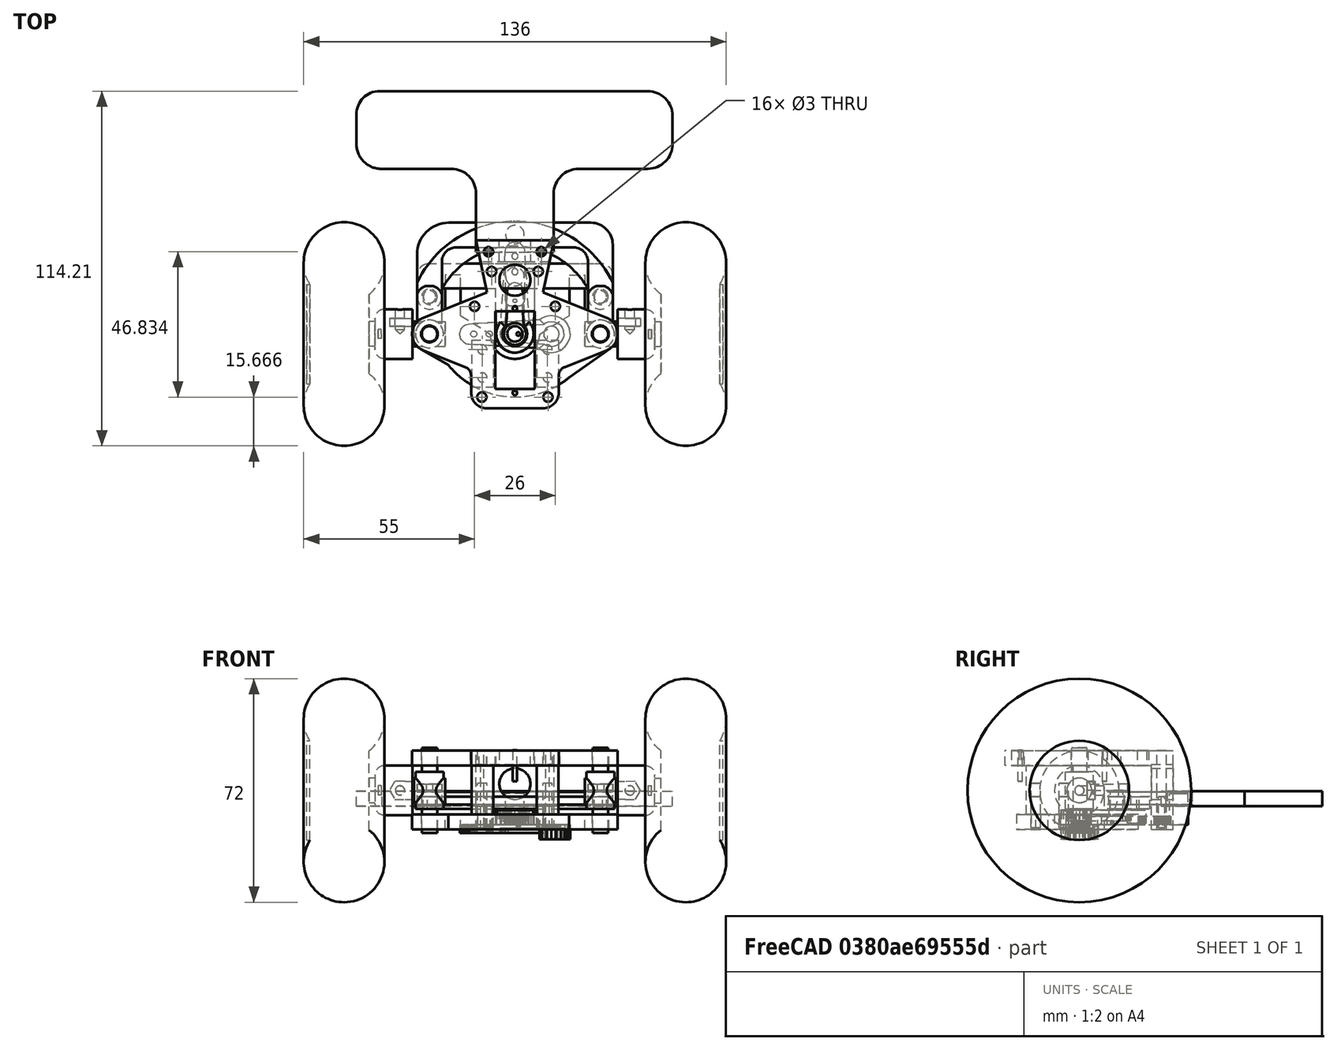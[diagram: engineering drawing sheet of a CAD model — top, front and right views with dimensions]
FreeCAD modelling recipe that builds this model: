
FCSTD DOCUMENT  (FreeCAD 0.18R16131 (Git))
Label: Direccion V2
License: All rights reserved
LicenseURL: http://en.wikipedia.org/wiki/All_rights_reserved
objects: Part::Cylinder×44, Part::MultiFuse×20, Sketcher::SketchObject×14, Part::Cut×10, PartDesign::Pad×9, Part::Feature×9, Part::Box×8, App::DocumentObjectGroup×7, Part::Fillet×6, Part::Extrusion×4, Mesh::Feature×2, Part::Torus×2, PartDesign::Pocket×1, PartDesign::Fillet×1
note: 138 computed .brp shape members not serialized (recipe doc carries the construction recipe); baked Part::Feature solids carry a one-line shape summary decoded from their .brp

FEATURE [Sketcher::SketchObject] Sketch  label="SketchB"
  MapMode = 5
  Placement = pos=(0,0,-1.5) rot=(0,0,1;0rad)
  sketch-geometry (23):
    g0: LineSegment StartX=-29.5785 StartY=5.19999 StartZ=0 EndX=-22.5 EndY=8.02935 EndZ=0
    g1: LineSegment StartX=22.5 StartY=8.02935 StartZ=0 EndX=29.5822 EndY=5.1985 EndZ=0
    g2: LineSegment StartX=30.743 StartY=-4.56538 StartZ=0 EndX=17.4375 EndY=-14.017 EndZ=0
    g3: LineSegment StartX=-21.4029 StartY=-10.0046 StartZ=0 EndX=-30.3074 EndY=-4.84546 EndZ=0
    g4: Circle CenterX=27.5 CenterY=0 CenterZ=0 NormalX=0 NormalY=0 NormalZ=1 AngleXU=0 Radius=2.7
    g5: Circle CenterX=-27.5 CenterY=0 CenterZ=0 NormalX=0 NormalY=0 NormalZ=1 AngleXU=0 Radius=2.7
    g6: ArcOfCircle CenterX=27.5 CenterY=0 CenterZ=0 NormalX=0 NormalY=0 NormalZ=1 AngleXU=0 Radius=5.6 StartAngle=5.33003 EndAngle=7.47301
    g7: ArcOfCircle CenterX=-27.5 CenterY=0 CenterZ=0 NormalX=0 NormalY=0 NormalZ=1 AngleXU=0 Radius=5.6 StartAngle=1.95105 EndAngle=4.18726
    g8: ArcOfCircle CenterX=0 CenterY=0 CenterZ=0 NormalX=0 NormalY=0 NormalZ=1 AngleXU=0 Radius=8 StartAngle=3.14159 EndAngle=6.28319
    g9: ArcOfCircle CenterX=0 CenterY=7.18175 CenterZ=0 NormalX=0 NormalY=0 NormalZ=1 AngleXU=0 Radius=27.4491 StartAngle=3.81816 EndAngle=5.40074
    g10: LineSegment StartX=-17.5 StartY=5.98295 StartZ=0 EndX=-8 EndY=-2.0002e-12 EndZ=0
    g11: LineSegment StartX=8 StartY=3e-12 StartZ=0 EndX=17.5 EndY=5.98295 EndZ=0
    g12: LineSegment StartX=-17.5 StartY=5.98295 StartZ=0 EndX=-17.5 EndY=18.983 EndZ=0
    g13: LineSegment StartX=-22.5 StartY=18.983 StartZ=0 EndX=-22.5 EndY=8.02935 EndZ=0
    g14: LineSegment StartX=-17.5 StartY=18.983 StartZ=0 EndX=-22.5 EndY=18.983 EndZ=0
    g15: LineSegment [constr] StartX=17.5 StartY=5.98295 StartZ=0 EndX=22.5 EndY=8.02935 EndZ=0
    g16: LineSegment StartX=17.5 StartY=5.98295 StartZ=0 EndX=17.5 EndY=18.983 EndZ=0
    g17: LineSegment StartX=17.5 StartY=18.983 StartZ=0 EndX=22.5 EndY=18.983 EndZ=0
    g18: LineSegment StartX=22.5 StartY=18.983 StartZ=0 EndX=22.5 EndY=8.02935 EndZ=0
    g19: Circle CenterX=10.5 CenterY=-4.99986 CenterZ=0 NormalX=0 NormalY=0 NormalZ=1 AngleXU=0 Radius=1.5
    g20: Circle CenterX=-10.5 CenterY=-4.99986 CenterZ=0 NormalX=0 NormalY=0 NormalZ=1 AngleXU=0 Radius=1.5
    g21: Circle CenterX=-10.5 CenterY=-13.9999 CenterZ=0 NormalX=0 NormalY=0 NormalZ=1 AngleXU=0 Radius=1.5
    g22: Circle CenterX=10.5 CenterY=-13.9999 CenterZ=0 NormalX=0 NormalY=0 NormalZ=1 AngleXU=0 Radius=1.5
  constraints (55):
    c: DistanceX(g5,g4) = 55
    c: Symmetric(g4,g5,g-2)
    c: PointOnObject(g4,g-1)
    c: Radius(g4) = 2.7
    c: Equal(g5,g4)
    c: Coincident(g6,g4)
    c: Coincident(g7,g5)
    c: Radius(g7) = 5.6
    c: Equal(g7,g6)
    c: DistanceY(g2,g11) = 20
    c: DistanceX(g10,g11) = 35
    c: Tangent(g2,g6) = 1.5708
    c: Tangent(g0,g7) = 1.5708
    c: Tangent(g3,g7) = 1.5708
    c: Coincident(g8,g-1)
    c: Radius(g8) = 8
    c: PointOnObject(g9,g-2)
    c: Coincident(g3,g9)
    c: PointOnObject(g8,g-1)
    c: PointOnObject(g8,g-1)
    c: Coincident(g10,g8)
    c: Coincident(g11,g8)
    c: Coincident(g12,g10)
    c: Vertical(g12)
    c: Vertical(g13)
    c: Coincident(g14,g12)
    c: Coincident(g14,g13)
    c: Horizontal(g14)
    c: Coincident(g0,g13)
    c: Symmetric(g10,g11,g-2)
    c: Symmetric(g1,g0,g-2)
    c: Coincident(g15,g11)
    c: Coincident(g6,g1)
    c: Coincident(g16,g11)
    c: Vertical(g16)
    c: PointOnObject(g18,g17)
    c: Vertical(g18)
    c: Coincident(g17,g18)
    c: DistanceX(g17,g17) = 5
    c: DistanceY(g16,g16) = 13
    c: Coincident(g16,g17)
    c: Horizontal(g17)
    c: Coincident(g15,g18)
    c: Coincident(g15,g1)
    c: Coincident(g9,g2)
    c: Equal(g12,g16)
    c: Radius(g19) = 1.5
    c: Equal(g19,g20)
    c: Equal(g20,g21)
    c: Equal(g21,g22)
    c: Symmetric(g20,g19,g-2)
    c: Symmetric(g21,g22,g-2)
    c: DistanceX(g20,g19) = 21
    c: DistanceX(g21,g22) = 21
    c: DistanceY(g21,g20) = 9
FEATURE [PartDesign::Pad] Pad  label="Carter superior"
  Length = 4.8
  Length2 = 100
  Placement = pos=(0,0,-1.5) rot=(0,0,1;0rad)
  Profile = -> Sketch
  Type = 0
FEATURE [Part::Cylinder] Cylinder  label="Cilindro"
  Angle = 360
  AttacherType = Attacher::AttachEngine3D
  Height = 27.5
  Placement = pos=(0,0,-13.75) rot=(0,0,1;0rad)
  Radius = 2.5
FEATURE [Part::Cylinder] Cylinder001  label="Cilindro001"
  Angle = 360
  AttacherType = Attacher::AttachEngine3D
  Height = 12
  Placement = pos=(0,0,-6) rot=(0,0,1;0rad)
  Radius = 4.5
FEATURE [Part::Cylinder] Cylinder002  label="Cilindro002"
  Angle = 360
  AttacherType = Attacher::AttachEngine3D
  Height = 10
  Placement = pos=(-5,0,0) rot=(0,1,0;1.5708rad)
  Radius = 4
FEATURE [Part::Cylinder] Cylinder003  label="Eje giro rueda 1"
  Angle = 360
  AttacherType = Attacher::AttachEngine3D
  Height = 20
  Placement = pos=(23,0,11) rot=(0,1,0;1.5708rad)
  Radius = 1.5
FEATURE [Part::Box] Box  label="Cubo"
  AttacherType = Attacher::AttachEngine3D
  Height = 2
  Length = 8
  Placement = pos=(-4,0,0) rot=(0,0,1;0rad)
  Width = 15.5
FEATURE [Sketcher::SketchObject] Sketch001
  MapMode = 5
  sketch-geometry (7):
    g0: ArcOfCircle CenterX=0 CenterY=11.4326 CenterZ=0 NormalX=0 NormalY=0 NormalZ=1 AngleXU=0 Radius=4.2 StartAngle=6.10025 EndAngle=9.60926
    g1: LineSegment StartX=4.12992 StartY=10.6686 StartZ=0 EndX=4.12444 EndY=10.639 EndZ=0
    g2: LineSegment StartX=4.12444 StartY=10.639 StartZ=0 EndX=5.59637 EndY=10.639 EndZ=0
    g3: LineSegment StartX=5.59637 StartY=10.639 StartZ=0 EndX=5.59637 EndY=16.9442 EndZ=0
    g4: LineSegment StartX=5.59637 StartY=16.9442 StartZ=0 EndX=-5.22917 EndY=16.9442 EndZ=0
    g5: LineSegment StartX=-5.22917 StartY=16.9442 StartZ=0 EndX=-5.22917 EndY=10.7807 EndZ=0
    g6: LineSegment StartX=-5.22917 StartY=10.7807 StartZ=0 EndX=-4.12873 EndY=10.6622 EndZ=0
  constraints (13):
    c: PointOnObject(g0,g-2)
    c: Radius(g0) = 4.2
    c: Tangent(g0,g1) = 1.5708
    c: Coincident(g1,g2)
    c: Horizontal(g2)
    c: Coincident(g2,g3)
    c: Vertical(g3)
    c: Coincident(g3,g4)
    c: Horizontal(g4)
    c: Coincident(g4,g5)
    c: Vertical(g5)
    c: Coincident(g5,g6)
    c: Coincident(g6,g0)
FEATURE [PartDesign::Pad] Pad001
  Length = 10
  Length2 = 100
  Profile = -> Sketch001
  Type = 0
FEATURE [Part::Cut] Cut
  Base = -> Box
  Tool = -> Pad001
FEATURE [Part::Cylinder] Cylinder004  label="Cilindro004"
  Angle = 360
  AttacherType = Attacher::AttachEngine3D
  Height = 7.5
  Placement = pos=(0,12,-6) rot=(0,0,1;0rad)
  Radius = 2
FEATURE [Part::Cylinder] Cylinder005  label="Cilindro005"
  Angle = 360
  AttacherType = Attacher::AttachEngine3D
  Height = 27.5
  Placement = pos=(0,0,-13.75) rot=(0,0,1;0rad)
  Radius = 2.5
FEATURE [Part::Cylinder] Cylinder006  label="Cilindro006"
  Angle = 360
  AttacherType = Attacher::AttachEngine3D
  Height = 12
  Placement = pos=(0,0,-6) rot=(0,0,1;0rad)
  Radius = 4.5
FEATURE [Part::Cylinder] Cylinder007  label="Cilindro007"
  Angle = 360
  AttacherType = Attacher::AttachEngine3D
  Height = 10
  Placement = pos=(-5,0,0) rot=(0,1,0;1.5708rad)
  Radius = 4
FEATURE [Part::Box] Box001  label="Cubo001"
  AttacherType = Attacher::AttachEngine3D
  Height = 2
  Length = 8
  Placement = pos=(-4,0,0) rot=(0,0,1;0rad)
  Width = 15.5
FEATURE [Sketcher::SketchObject] Sketch002
  MapMode = 5
  sketch-geometry (7):
    g0: ArcOfCircle CenterX=0 CenterY=11.4326 CenterZ=0 NormalX=0 NormalY=0 NormalZ=1 AngleXU=0 Radius=4.2 StartAngle=6.10025 EndAngle=9.60926
    g1: LineSegment StartX=4.12992 StartY=10.6686 StartZ=0 EndX=4.12444 EndY=10.639 EndZ=0
    g2: LineSegment StartX=4.12444 StartY=10.639 StartZ=0 EndX=5.59637 EndY=10.639 EndZ=0
    g3: LineSegment StartX=5.59637 StartY=10.639 StartZ=0 EndX=5.59637 EndY=16.9442 EndZ=0
    g4: LineSegment StartX=5.59637 StartY=16.9442 StartZ=0 EndX=-5.22917 EndY=16.9442 EndZ=0
    g5: LineSegment StartX=-5.22917 StartY=16.9442 StartZ=0 EndX=-5.22917 EndY=10.7807 EndZ=0
    g6: LineSegment StartX=-5.22917 StartY=10.7807 StartZ=0 EndX=-4.12873 EndY=10.6622 EndZ=0
  constraints (13):
    c: PointOnObject(g0,g-2)
    c: Radius(g0) = 4.2
    c: Tangent(g0,g1) = 1.5708
    c: Coincident(g1,g2)
    c: Horizontal(g2)
    c: Coincident(g2,g3)
    c: Vertical(g3)
    c: Coincident(g3,g4)
    c: Horizontal(g4)
    c: Coincident(g4,g5)
    c: Vertical(g5)
    c: Coincident(g5,g6)
    c: Coincident(g6,g0)
FEATURE [PartDesign::Pad] Pad002
  Length = 10
  Length2 = 100
  Profile = -> Sketch002
  Type = 0
FEATURE [Part::Cut] Cut001
  Base = -> Box001
  Tool = -> Pad002
FEATURE [Part::Cylinder] Cylinder008  label="Cilindro008"
  Angle = 360
  AttacherType = Attacher::AttachEngine3D
  Height = 7.5
  Placement = pos=(0,12,-6) rot=(0,0,1;0rad)
  Radius = 2
FEATURE [Part::Cylinder] Cylinder009  label="Eje giro rueda 2"
  Angle = 360
  AttacherType = Attacher::AttachEngine3D
  Height = 20
  Placement = pos=(-43,0,11) rot=(0,1,0;1.5708rad)
  Radius = 1.5
FEATURE [Part::MultiFuse] Fusion  label="Eje giro direccion 1"
  Placement = pos=(27.5,0,11) rot=(0,0,1;0rad)
  Shapes = -> [Cylinder,Cylinder001,Cylinder002,Cut,Cylinder004]
FEATURE [Part::MultiFuse] Fusion001  label="Eje giro direccion 2"
  Placement = pos=(-27.5,0,11) rot=(0,0,1;0rad)
  Shapes = -> [Cylinder005,Cylinder006,Cylinder007,Cut001,Cylinder008]
FEATURE [Sketcher::SketchObject] Sketch003
  MapMode = 5
  Placement = pos=(0,12,1.5) rot=(0,0,1;0rad)
  Support = -> [Cylinder008]
  sketch-geometry (12):
    g0: LineSegment StartX=-23.5 StartY=0 StartZ=0 EndX=-23.5 EndY=11.3304 EndZ=0
    g1: LineSegment StartX=-18.9625 StartY=15.8679 StartZ=0 EndX=18.9404 EndY=15.8679 EndZ=0
    g2: LineSegment StartX=23.5 StartY=11.3083 StartZ=0 EndX=23.5 EndY=0 EndZ=0
    g3: LineSegment StartX=31.5 StartY=0 StartZ=0 EndX=31.5 EndY=16.7855 EndZ=0
    g4: LineSegment StartX=24.4177 StartY=23.8679 StartZ=0 EndX=-21.2655 EndY=23.8679 EndZ=0
    g5: LineSegment StartX=-31.5 StartY=13.6334 StartZ=0 EndX=-31.5 EndY=0 EndZ=0
    g6: ArcOfCircle CenterX=27.5 CenterY=0 CenterZ=0 NormalX=0 NormalY=0 NormalZ=1 AngleXU=0 Radius=4 StartAngle=3.14159 EndAngle=6.28319
    g7: ArcOfCircle CenterX=-27.5 CenterY=0 CenterZ=0 NormalX=0 NormalY=0 NormalZ=1 AngleXU=0 Radius=4 StartAngle=3.14159 EndAngle=6.28319
    g8: ArcOfCircle CenterX=-21.2655 CenterY=13.6334 CenterZ=0 NormalX=0 NormalY=0 NormalZ=1 AngleXU=0 Radius=10.2345 StartAngle=1.5708 EndAngle=3.14159
    g9: ArcOfCircle CenterX=-18.9625 CenterY=11.3304 CenterZ=0 NormalX=0 NormalY=0 NormalZ=1 AngleXU=0 Radius=4.53751 StartAngle=1.5708 EndAngle=3.14159
    g10: ArcOfCircle CenterX=24.4177 CenterY=16.7855 CenterZ=0 NormalX=0 NormalY=0 NormalZ=1 AngleXU=0 Radius=7.08234 StartAngle=0 EndAngle=1.5708
    g11: ArcOfCircle CenterX=18.9404 CenterY=11.3083 CenterZ=0 NormalX=0 NormalY=0 NormalZ=1 AngleXU=0 Radius=4.55958 StartAngle=0 EndAngle=1.5708
  constraints (30):
    c: Vertical(g0)
    c: Horizontal(g1)
    c: Vertical(g3)
    c: Horizontal(g4)
    c: Vertical(g5)
    c: DistanceX(g5,g0) = 8
    c: Vertical(g2)
    c: PointOnObject(g6,g-1)
    c: Tangent(g6,g3) = -1.5708
    c: Coincident(g3,g6)
    c: Tangent(g6,g2) = -1.5708
    c: Radius(g6) = 4
    c: Coincident(g2,g6)
    c: PointOnObject(g7,g-1)
    c: Tangent(g7,g5) = -1.5708
    c: Tangent(g7,g0) = -1.5708
    c: Coincident(g5,g7)
    c: Coincident(g0,g7)
    c: Radius(g7) = 4
    c: Tangent(g5,g8) = -1.5708
    c: Tangent(g4,g8) = -1.5708
    c: Tangent(g0,g9) = 1.5708
    c: Tangent(g1,g9) = 1.5708
    c: Tangent(g3,g10) = -1.5708
    c: Tangent(g4,g10) = -1.5708
    c: Tangent(g2,g11) = 1.5708
    c: Tangent(g1,g11) = 1.5708
    c: DistanceY(g1,g4) = 8
    c: Symmetric(g5,g3,g-2)
    c: DistanceX(g0,g2) = 47
FEATURE [Part::Extrusion] Extrude  label="Barra direccion"
  Base = -> Sketch003
  Dir = (0,0,4)
  DirMode = 0
  FaceMakerClass = Part::FaceMakerExtrusion
  LengthFwd = 0
  LengthRev = 0
  Placement = pos=(0,0,5) rot=(0,0,1;0rad)
  Solid = true
  Symmetric = false
FEATURE [Part::Cylinder] Cylinder010  label="Cilindro009"
  Angle = 360
  AttacherType = Attacher::AttachEngine3D
  Height = 7.5
  Placement = pos=(-27.5,12,5) rot=(0,0,1;0rad)
  Radius = 2.5
FEATURE [Part::Cylinder] Cylinder011  label="Cilindro010"
  Angle = 360
  AttacherType = Attacher::AttachEngine3D
  Height = 7.5
  Placement = pos=(27.5,12,5) rot=(0,0,1;0rad)
  Radius = 2.5
FEATURE [Part::MultiFuse] Fusion002
  Shapes = -> [Cylinder010,Cylinder011]
FEATURE [Part::Cut] Cut002  label="Barra Dir"
  Base = -> Extrude
  Tool = -> Fusion002
FEATURE [Mesh::Feature] Servo_SG90  label="Servo-SG90"
  Placement = pos=(0,-16.5,33.5) rot=(0,1,0;3.14159rad)
FEATURE [Part::Cylinder] Cylinder012  label="Cilindro011"
  Angle = 360
  AttacherType = Attacher::AttachEngine3D
  Height = 20
  Placement = pos=(47,0,11) rot=(0,1,0;1.5708rad)
  Radius = 16
FEATURE [Part::Cylinder] Cylinder013  label="Cilindro012"
  Angle = 360
  AttacherType = Attacher::AttachEngine3D
  Height = 20
  Placement = pos=(-67,0,11) rot=(0,1,0;1.5708rad)
  Radius = 16
FEATURE [Part::Torus] Torus  label="Toro"
  Angle1 = -180
  Angle2 = 180
  Angle3 = 360
  AttacherType = Attacher::AttachEngine3D
  Placement = pos=(-55,0,11) rot=(0,1,0;1.5708rad)
  Radius1 = 23
  Radius2 = 13
FEATURE [Part::Torus] Torus001  label="Toro001"
  Angle1 = -180
  Angle2 = 180
  Angle3 = 360
  AttacherType = Attacher::AttachEngine3D
  Placement = pos=(55,0,11) rot=(0,1,0;1.5708rad)
  Radius1 = 23
  Radius2 = 13
FEATURE [Part::Cylinder] Cylinder014  label="Cilindro013"
  Angle = 360
  AttacherType = Attacher::AttachEngine3D
  Height = 12
  Radius = 8
FEATURE [Part::Cylinder] Cylinder015  label="Taladro"
  Angle = 360
  AttacherType = Attacher::AttachEngine3D
  Height = 11
  Radius = 1.5
FEATURE [Part::Cylinder] Cylinder016  label="Cilindro014"
  Angle = 360
  AttacherType = Attacher::AttachEngine3D
  Height = 2
  Placement = pos=(0,0,12) rot=(0,0,1;0rad)
  Radius = 4
FEATURE [Part::Box] Box002  label="Cubo002"
  AttacherType = Attacher::AttachEngine3D
  Height = 15
  Length = 1.7
  Placement = pos=(-0.85,-2.3,22) rot=(0,0,1;0rad)
  Width = 4.6
FEATURE [Part::Box] Box003  label="Cubo003"
  AttacherType = Attacher::AttachEngine3D
  Height = 15
  Length = 4.6
  Placement = pos=(-2.3,-0.85,22) rot=(0,0,1;0rad)
  Width = 1.7
FEATURE [Part::Fillet] Fillet
  Base = -> Box002
  Edges = 2 edges r=1: [Edge10,Edge12]
FEATURE [Part::Fillet] Fillet001
  Base = -> Box003
  Edges = 2 edges r=1: [Edge2,Edge6]
FEATURE [Part::MultiFuse] Fusion003
  Placement = pos=(0,0,-8) rot=(0,0,1;0rad)
  Shapes = -> [Fillet,Fillet001]
FEATURE [Part::Cylinder] Cylinder017  label="Taladro tornillo"
  Angle = 360
  AttacherType = Attacher::AttachEngine3D
  Height = 10
  Placement = pos=(0,0,4) rot=(-1,0,0;1.5708rad)
  Radius = 1.5
FEATURE [Sketcher::SketchObject] Sketch004
  MapMode = 5
  Placement = pos=(0,5,-2) rot=(1,0,0;1.5708rad)
  sketch-geometry (8):
    g0: LineSegment StartX=0 StartY=9.41258 StartZ=0 EndX=-2.88764 EndY=7.71686 EndZ=0
    g1: LineSegment StartX=-2.88764 StartY=7.71686 StartZ=0 EndX=-2.86293 EndY=4.36823 EndZ=0
    g2: LineSegment StartX=2.93707 StartY=4.41103 StartZ=0 EndX=2.91236 EndY=7.75966 EndZ=0
    g3: LineSegment StartX=2.91236 StartY=7.75966 StartZ=0 EndX=0 EndY=9.41258 EndZ=0
    g4: Circle [constr] CenterX=0.0247135 CenterY=6.06395 CenterZ=0 NormalX=0 NormalY=0 NormalZ=1 AngleXU=0 Radius=3.34872
    g5: LineSegment StartX=-2.86293 StartY=4.36823 StartZ=0 EndX=-2.86293 EndY=0 EndZ=0
    g6: LineSegment StartX=2.93707 StartY=4.41103 StartZ=0 EndX=2.93707 EndY=0 EndZ=0
    g7: LineSegment StartX=-2.86293 StartY=0 StartZ=0 EndX=2.93707 EndY=0 EndZ=0
  constraints (22):
    c: Coincident(g0,g1)
    c: Coincident(g2,g3)
    c: Coincident(g3,g0)
    c: Equal(g0,g1)
    c: Equal(g0,g2)
    c: Equal(g0,g3)
    c: PointOnObject(g0,g4)
    c: PointOnObject(g1,g4)
    c: PointOnObject(g2,g4)
    c: PointOnObject(g2,g4)
    c: PointOnObject(g3,g4)
    c: PointOnObject(g0,g-2)
    c: DistanceX(g0,g2) = 5.8
    c: Symmetric(g1,g2,g4)
    c: Coincident(g5,g1)
    c: PointOnObject(g5,g-1)
    c: Vertical(g5)
    c: Vertical(g6)
    c: Coincident(g7,g5)
    c: Coincident(g7,g6)
    c: Horizontal(g7)
    c: Coincident(g6,g2)
FEATURE [PartDesign::Pad] Pad003  label="Tuerca"
  Length = 2.5
  Length2 = 100
  Placement = pos=(0,5,-2) rot=(1,0,0;1.5708rad)
  Profile = -> Sketch004
  Type = 0
FEATURE [Part::MultiFuse] Fusion004  label="Hueco"
  Shapes = -> [Cylinder015,Cylinder017,Pad003]
FEATURE [Part::Fillet] Fillet002  label="Base"
  Base = -> Cylinder014
  Edges = 1 edges r=3: [Edge1]
FEATURE [Part::Cut] Cut003  label="Base2"
  Base = -> Fillet002
  Tool = -> Fusion004
FEATURE [Part::MultiFuse] Fusion005  label="Eje rueda delantera 1"
  Placement = pos=(33,0,11) rot=(0,1,0;1.5708rad)
  Shapes = -> [Cut003,Cylinder016,Fusion003]
FEATURE [Part::Cylinder] Cylinder018  label="Cilindro015"
  Angle = 360
  AttacherType = Attacher::AttachEngine3D
  Height = 12
  Radius = 8
FEATURE [Part::Cylinder] Cylinder019  label="Taladro001"
  Angle = 360
  AttacherType = Attacher::AttachEngine3D
  Height = 11
  Radius = 1.5
FEATURE [Part::Cylinder] Cylinder020  label="Cilindro016"
  Angle = 360
  AttacherType = Attacher::AttachEngine3D
  Height = 2
  Placement = pos=(0,0,12) rot=(0,0,1;0rad)
  Radius = 4
FEATURE [Part::Box] Box004  label="Cubo004"
  AttacherType = Attacher::AttachEngine3D
  Height = 15
  Length = 1.7
  Placement = pos=(-0.85,-2.3,22) rot=(0,0,1;0rad)
  Width = 4.6
FEATURE [Part::Box] Box005  label="Cubo005"
  AttacherType = Attacher::AttachEngine3D
  Height = 15
  Length = 4.6
  Placement = pos=(-2.3,-0.85,22) rot=(0,0,1;0rad)
  Width = 1.7
FEATURE [Part::Fillet] Fillet003
  Base = -> Box004
  Edges = 2 edges r=1: [Edge10,Edge12]
FEATURE [Part::Fillet] Fillet004
  Base = -> Box005
  Edges = 2 edges r=1: [Edge2,Edge6]
FEATURE [Part::MultiFuse] Fusion006
  Placement = pos=(0,0,-8) rot=(0,0,1;0rad)
  Shapes = -> [Fillet003,Fillet004]
FEATURE [Part::Cylinder] Cylinder021  label="Taladro tornillo001"
  Angle = 360
  AttacherType = Attacher::AttachEngine3D
  Height = 10
  Placement = pos=(0,0,4) rot=(-1,0,0;1.5708rad)
  Radius = 1.5
FEATURE [Sketcher::SketchObject] Sketch005
  MapMode = 5
  Placement = pos=(0,5,-2) rot=(1,0,0;1.5708rad)
  sketch-geometry (8):
    g0: LineSegment StartX=0 StartY=9.41258 StartZ=0 EndX=-2.88764 EndY=7.71686 EndZ=0
    g1: LineSegment StartX=-2.88764 StartY=7.71686 StartZ=0 EndX=-2.86293 EndY=4.36823 EndZ=0
    g2: LineSegment StartX=2.93707 StartY=4.41103 StartZ=0 EndX=2.91236 EndY=7.75966 EndZ=0
    g3: LineSegment StartX=2.91236 StartY=7.75966 StartZ=0 EndX=0 EndY=9.41258 EndZ=0
    g4: Circle [constr] CenterX=0.0247135 CenterY=6.06395 CenterZ=0 NormalX=0 NormalY=0 NormalZ=1 AngleXU=0 Radius=3.34872
    g5: LineSegment StartX=-2.86293 StartY=4.36823 StartZ=0 EndX=-2.86293 EndY=0 EndZ=0
    g6: LineSegment StartX=2.93707 StartY=4.41103 StartZ=0 EndX=2.93707 EndY=0 EndZ=0
    g7: LineSegment StartX=-2.86293 StartY=0 StartZ=0 EndX=2.93707 EndY=0 EndZ=0
  constraints (22):
    c: Coincident(g0,g1)
    c: Coincident(g2,g3)
    c: Coincident(g3,g0)
    c: Equal(g0,g1)
    c: Equal(g0,g2)
    c: Equal(g0,g3)
    c: PointOnObject(g0,g4)
    c: PointOnObject(g1,g4)
    c: PointOnObject(g2,g4)
    c: PointOnObject(g2,g4)
    c: PointOnObject(g3,g4)
    c: PointOnObject(g0,g-2)
    c: DistanceX(g0,g2) = 5.8
    c: Symmetric(g1,g2,g4)
    c: Coincident(g5,g1)
    c: PointOnObject(g5,g-1)
    c: Vertical(g5)
    c: Vertical(g6)
    c: Coincident(g7,g5)
    c: Coincident(g7,g6)
    c: Horizontal(g7)
    c: Coincident(g6,g2)
FEATURE [PartDesign::Pad] Pad004  label="Tuerca001"
  Length = 2.5
  Length2 = 100
  Placement = pos=(0,5,-2) rot=(1,0,0;1.5708rad)
  Profile = -> Sketch005
  Type = 0
FEATURE [Part::MultiFuse] Fusion007  label="Hueco001"
  Shapes = -> [Cylinder019,Cylinder021,Pad004]
FEATURE [Part::Fillet] Fillet005  label="Base003"
  Base = -> Cylinder018
  Edges = 1 edges r=3: [Edge1]
FEATURE [Part::Cut] Cut004  label="Base004"
  Base = -> Fillet005
  Tool = -> Fusion007
FEATURE [Part::MultiFuse] Fusion008  label="Eje rueda delantera 2"
  Placement = pos=(-33,0,11) rot=(0,-1,0;1.5708rad)
  Shapes = -> [Cut004,Cylinder020,Fusion006]
FEATURE [Part::MultiFuse] Fusion009
  Placement = pos=(3.6e-15,1.07e-14,0) rot=(0,0,1;0rad)
  Shapes = -> [Cylinder013,Torus,Fusion001,Cylinder009,Fusion008]
FEATURE [App::DocumentObjectGroup] Grupo001  label="Rueda 2"
  Group = -> [Fusion009]
FEATURE [Part::MultiFuse] Fusion010
  Placement = pos=(-3.6e-15,-1.07e-14,0) rot=(0,0,1;0rad)
  Shapes = -> [Cylinder012,Torus001,Fusion,Cylinder003,Fusion005]
FEATURE [App::DocumentObjectGroup] Grupo  label="Rueda 1"
  Group = -> [Fusion010]
FEATURE [Sketcher::SketchObject] Sketch006
  MapMode = 5
  Placement = pos=(0,12,1.5) rot=(0,0,1;0rad)
  Support = -> [Cylinder008]
  sketch-geometry (13):
    g0: ArcOfCircle CenterX=27.5 CenterY=0 CenterZ=0 NormalX=0 NormalY=0 NormalZ=1 AngleXU=0 Radius=4 StartAngle=3.14159 EndAngle=6.28319
    g1: ArcOfCircle CenterX=-27.5 CenterY=0 CenterZ=0 NormalX=0 NormalY=0 NormalZ=1 AngleXU=0 Radius=4 StartAngle=3.14159 EndAngle=6.28319
    g2: GeomPoint [constr] X=-0.022332 Y=22.2995 Z=0
    g3: GeomPoint [constr] X=0.308692 Y=14.2995 Z=0
    g4: GeomPoint [constr] X=0 Y=-10.7005 Z=0
    g5: GeomPoint [constr] X=0 Y=-2.70048 Z=0
    g6: LineSegment [constr] StartX=-48.5447 StartY=24.2365 StartZ=0 EndX=42.467 EndY=24.2365 EndZ=0
    g7: ArcOfCircle CenterX=0 CenterY=-10.7005 CenterZ=0 NormalX=0 NormalY=0 NormalZ=1 AngleXU=0 Radius=27 StartAngle=0.514842 EndAngle=2.62675
    g8: ArcOfCircle CenterX=0 CenterY=-10.7005 CenterZ=0 NormalX=0 NormalY=0 NormalZ=1 AngleXU=0 Radius=35 StartAngle=0.451027 EndAngle=2.69057
    g9: LineSegment StartX=-31.5 StartY=0 StartZ=0 EndX=-31.5 EndY=4.55567 EndZ=0
    g10: LineSegment StartX=-23.5 StartY=0 StartZ=0 EndX=-23.5 EndY=2.59426 EndZ=0
    g11: LineSegment StartX=23.5 StartY=0 StartZ=0 EndX=23.5 EndY=2.59426 EndZ=0
    g12: LineSegment StartX=31.5 StartY=0 StartZ=0 EndX=31.5 EndY=4.55567 EndZ=0
  constraints (28):
    c: DistanceX(g1,g1) = 8
    c: PointOnObject(g0,g-1)
    c: Radius(g0) = 4
    c: PointOnObject(g1,g-1)
    c: Symmetric(g1,g0,g-2)
    c: DistanceX(g1,g0) = 47
    c: PointOnObject(g4,g-2)
    c: DistanceY(g4,g3) = 25
    c: DistanceY(g3,g2) = 8
    c: Horizontal(g6)
    c: DistanceY(g4,g5) = 8
    c: PointOnObject(g5,g-2)
    c: Coincident(g7,g4)
    c: Coincident(g8,g4)
    c: Radius(g7) = 27
    c: Radius(g8) = 35
    c: Coincident(g9,g1)
    c: Vertical(g9)
    c: Coincident(g10,g1)
    c: Vertical(g10)
    c: Coincident(g11,g0)
    c: Vertical(g11)
    c: Coincident(g12,g0)
    c: Vertical(g12)
    c: Coincident(g12,g8)
    c: Coincident(g11,g7)
    c: Coincident(g7,g10)
    c: Coincident(g9,g8)
FEATURE [Part::Extrusion] Extrude001
  Base = -> Sketch006
  Dir = (0,0,4)
  DirMode = 0
  FaceMakerClass = Part::FaceMakerExtrusion
  LengthFwd = 0
  LengthRev = 0
  Placement = pos=(0,0,5) rot=(0,0,1;0rad)
  Solid = true
  Symmetric = false
FEATURE [Part::Cylinder] Cylinder022  label="Cilindro017"
  Angle = 360
  AttacherType = Attacher::AttachEngine3D
  Height = 7.5
  Placement = pos=(-27.5,12,5) rot=(0,0,1;0rad)
  Radius = 2.5
FEATURE [Part::Cylinder] Cylinder023  label="Cilindro018"
  Angle = 360
  AttacherType = Attacher::AttachEngine3D
  Height = 7.5
  Placement = pos=(27.5,12,5) rot=(0,0,1;0rad)
  Radius = 2.5
FEATURE [Part::MultiFuse] Fusion011
  Shapes = -> [Cylinder022,Cylinder023]
FEATURE [Part::Cut] Cut005
  Base = -> Extrude001
  Tool = -> Fusion011
FEATURE [Part::Cylinder] Cylinder024  label="Cilindro019"
  Angle = 360
  AttacherType = Attacher::AttachEngine3D
  Height = 10
  Placement = pos=(0,32,0) rot=(0,0,1;0rad)
  Radius = 3
FEATURE [App::DocumentObjectGroup] Grupo002  label="Barra direccion 2"
  Group = -> [Cut005,Cylinder024]
FEATURE [Sketcher::SketchObject] Sketch007
  MapMode = 5
  Placement = pos=(0,12,1.5) rot=(0,0,1;0rad)
  Support = -> [Cylinder008]
  sketch-geometry (10):
    g0: ArcOfCircle CenterX=27.5 CenterY=0 CenterZ=0 NormalX=0 NormalY=0 NormalZ=1 AngleXU=0 Radius=4 StartAngle=3.14159 EndAngle=6.28319
    g1: ArcOfCircle CenterX=-27.5 CenterY=0 CenterZ=0 NormalX=0 NormalY=0 NormalZ=1 AngleXU=0 Radius=4 StartAngle=3.14159 EndAngle=6.28319
    g2: LineSegment StartX=-23.5 StartY=2.66215 StartZ=0 EndX=23.5 EndY=2.66215 EndZ=0
    g3: LineSegment StartX=-28.1833 StartY=10.6622 StartZ=0 EndX=28.1833 EndY=10.6622 EndZ=0
    g4: LineSegment StartX=23.5 StartY=-1e-12 StartZ=0 EndX=23.5 EndY=2.66215 EndZ=0
    g5: LineSegment StartX=-23.5 StartY=0 StartZ=0 EndX=-23.5 EndY=2.66215 EndZ=0
    g6: LineSegment StartX=-31.5 StartY=2e-12 StartZ=0 EndX=-31.5 EndY=6.49244 EndZ=0
    g7: LineSegment StartX=31.5 StartY=2e-12 StartZ=0 EndX=31.5 EndY=7.29309 EndZ=0
    g8: ArcOfCircle CenterX=27.5422 CenterY=6.71386 CenterZ=0 NormalX=0 NormalY=0 NormalZ=1 AngleXU=0 Radius=4 StartAngle=0.145318 EndAngle=1.40983
    g9: ArcOfCircle CenterX=-27.5065 CenterY=6.71983 CenterZ=0 NormalX=0 NormalY=0 NormalZ=1 AngleXU=0 Radius=4 StartAngle=1.74081 EndAngle=3.19847
  constraints (26):
    c: DistanceX(g1,g1) = 8
    c: PointOnObject(g0,g-1)
    c: Radius(g0) = 4
    c: PointOnObject(g1,g-1)
    c: Symmetric(g1,g0,g-2)
    c: DistanceX(g1,g0) = 47
    c: Horizontal(g2)
    c: Horizontal(g3)
    c: DistanceY(g2,g3) = 8
    c: Coincident(g4,g0)
    c: Vertical(g4)
    c: Coincident(g5,g1)
    c: Coincident(g6,g1)
    c: Vertical(g6)
    c: Coincident(g7,g0)
    c: Vertical(g7)
    c: Coincident(g9,g6)
    c: Radius(g9) = 4
    c: Equal(g8,g9)
    c: Coincident(g9,g3)
    c: Coincident(g3,g8)
    c: Symmetric(g3,g3,g-2)
    c: Coincident(g4,g2)
    c: Vertical(g5)
    c: Coincident(g5,g2)
    c: Coincident(g7,g8)
FEATURE [Part::Extrusion] Extrude002
  Base = -> Sketch007
  Dir = (0,0,4)
  DirMode = 0
  FaceMakerClass = Part::FaceMakerExtrusion
  LengthFwd = 0
  LengthRev = 0
  Solid = true
  Symmetric = false
FEATURE [Part::Cylinder] Cylinder025  label="Cilindro020"
  Angle = 360
  AttacherType = Attacher::AttachEngine3D
  Height = 7.5
  Placement = pos=(-27.5,12,5) rot=(0,0,1;0rad)
  Radius = 2.1
FEATURE [Part::Cylinder] Cylinder026  label="Cilindro021"
  Angle = 360
  AttacherType = Attacher::AttachEngine3D
  Height = 7.5
  Placement = pos=(27.5,12,5) rot=(0,0,1;0rad)
  Radius = 2.1
FEATURE [Part::MultiFuse] Fusion012
  Placement = pos=(0,0,-6) rot=(0,0,1;0rad)
  Shapes = -> [Cylinder025,Cylinder026,Sketch007]
FEATURE [Part::Cut] Cut006
  Base = -> Extrude002
  Placement = pos=(0,0,5) rot=(0,0,1;0rad)
  Tool = -> Fusion012
FEATURE [Part::Cylinder] Cylinder027  label="Cilindro022"
  Angle = 360
  AttacherType = Attacher::AttachEngine3D
  Height = 8
  Placement = pos=(0,18.5,2) rot=(0,0,1;0rad)
  Radius = 3
FEATURE [Part::MultiFuse] Fusion013
  Placement = pos=(0,0,-1.5) rot=(0,0,1;0rad)
  Shapes = -> [Cut006,Cylinder027]
FEATURE [App::DocumentObjectGroup] Grupo003  label="Barra direccion 3"
  Group = -> [Fusion013]
FEATURE [Sketcher::SketchObject] Sketch009
  MapMode = 5
  Placement = pos=(0,0,6) rot=(0,0,1;0rad)
  sketch-geometry (15):
    g0: LineSegment StartX=-12.5 StartY=45.2071 StartZ=0 EndX=-12.5 EndY=26.3976 EndZ=0
    g1: LineSegment StartX=-12.5 StartY=26.3976 StartZ=0 EndX=12.5 EndY=26.3976 EndZ=0
    g2: LineSegment StartX=12.5 StartY=26.3976 StartZ=0 EndX=12.5 EndY=45.2071 EndZ=0
    g3: LineSegment StartX=20.5 StartY=53.2071 StartZ=0 EndX=42.7574 EndY=53.2071 EndZ=0
    g4: LineSegment StartX=50.7574 StartY=61.2071 StartZ=0 EndX=50.7574 EndY=70.2071 EndZ=0
    g5: LineSegment StartX=42.7574 StartY=78.2071 StartZ=0 EndX=-43.5536 EndY=78.2071 EndZ=0
    g6: LineSegment StartX=-51.0231 StartY=70.7377 StartZ=0 EndX=-51.0231 EndY=61.2027 EndZ=0
    g7: ArcOfCircle CenterX=-43.0231 CenterY=61.2027 CenterZ=0 NormalX=0 NormalY=0 NormalZ=1 AngleXU=0 Radius=8 StartAngle=3.14159 EndAngle=4.7456
    g8: ArcOfCircle CenterX=-43.5536 CenterY=70.7377 CenterZ=0 NormalX=0 NormalY=0 NormalZ=1 AngleXU=0 Radius=7.46949 StartAngle=1.5708 EndAngle=3.14159
    g9: ArcOfCircle CenterX=42.7574 CenterY=70.2071 CenterZ=0 NormalX=0 NormalY=0 NormalZ=1 AngleXU=0 Radius=8 StartAngle=0 EndAngle=1.5708
    g10: ArcOfCircle CenterX=42.7574 CenterY=61.2071 CenterZ=0 NormalX=0 NormalY=0 NormalZ=1 AngleXU=0 Radius=8 StartAngle=4.71239 EndAngle=6.28319
    g11: ArcOfCircle CenterX=20.5 CenterY=45.2071 CenterZ=0 NormalX=0 NormalY=0 NormalZ=1 AngleXU=0 Radius=8 StartAngle=1.5708 EndAngle=3.14159
    g12: LineSegment StartX=-42.7574 StartY=53.2071 StartZ=0 EndX=-20.5 EndY=53.2071 EndZ=0
    g13: ArcOfCircle CenterX=-20.5 CenterY=45.2071 CenterZ=0 NormalX=0 NormalY=0 NormalZ=1 AngleXU=0 Radius=8 StartAngle=0 EndAngle=1.5708
    g14: Circle [constr] CenterX=27.7123 CenterY=-0.255807 CenterZ=0 NormalX=0 NormalY=0 NormalZ=1 AngleXU=0 Radius=49.0446
  constraints (31):
    c: Coincident(g0,g1)
    c: Coincident(g1,g2)
    c: Horizontal(g1)
    c: Vertical(g0)
    c: Vertical(g2)
    c: Horizontal(g3)
    c: Horizontal(g5)
    c: Vertical(g4)
    c: Vertical(g6)
    c: DistanceX(g1,g1) = 25
    c: Symmetric(g1,g0,g-2)
    c: Tangent(g6,g7) = -1.5708
    c: Tangent(g6,g8) = -1.5708
    c: Tangent(g5,g8) = -1.5708
    c: Tangent(g5,g9) = -1.5708
    c: Tangent(g4,g9) = -1.5708
    c: Tangent(g4,g10) = -1.5708
    c: Tangent(g3,g10) = -1.5708
    c: Tangent(g3,g11) = 1.5708
    c: Tangent(g2,g11) = 1.5708
    c: Horizontal(g12)
    c: Tangent(g12,g13) = 1.5708
    c: Tangent(g0,g13) = 1.5708
    c: Radius(g11) = 8
    c: Equal(g11,g13)
    c: Radius(g10) = 8
    c: Equal(g9,g10)
    c: Coincident(g7,g12)
    c: Equal(g7,g10)
    c: DistanceY(g7,g5) = 25
    c: Symmetric(g7,g3,g-2)
FEATURE [PartDesign::Pad] Pad005  label="bastidor"
  Length = 4.8
  Length2 = 100
  Placement = pos=(0,0,6) rot=(0,0,1;0rad)
  Profile = -> Sketch009
  Type = 0
FEATURE [Part::Feature] Face
  shape: bbox 25 x 2e-07 x 4.8 mm, 1 faces, 0 solids (baked)
FEATURE [Part::Feature] Face001
  shape: bbox 18 x 2e-07 x 4.8 mm, 1 faces, 0 solids (baked)
FEATURE [Part::Feature] Face002
  shape: bbox 25 x 12.92 x 12 mm, 1 faces, 0 solids (baked)
FEATURE [Part::Feature] Face003
  shape: bbox 25 x 12.92 x 12 mm, 1 faces, 0 solids (baked)
FEATURE [Part::Feature] Face004
  shape: bbox 3.5 x 12.92 x 16.8 mm, 1 faces, 0 solids (baked)
FEATURE [Part::Feature] Face005
  shape: bbox 3.5 x 12.92 x 16.8 mm, 1 faces, 0 solids (baked)
FEATURE [App::DocumentObjectGroup] Grupo005  label="Union Bastidor"
  Group = -> [Face,Face001,Face002,Face003,Face004,Face005]
FEATURE [Part::Box] Box006  label="Cubo006"
  AttacherType = Attacher::AttachEngine3D
  Height = 18
  Length = 7
  Placement = pos=(-14,-17,3.3) rot=(0,0,1;0rad)
  Width = 15
FEATURE [Part::Box] Box007  label="Cubo007"
  AttacherType = Attacher::AttachEngine3D
  Height = 18
  Length = 7
  Placement = pos=(7,-17,3.3) rot=(0,0,1;0rad)
  Width = 15
FEATURE [Sketcher::SketchObject] Sketch011
  MapMode = 5
  Placement = pos=(0,0,-1.6) rot=(0,0,1;0rad)
  sketch-geometry (4):
    g0: LineSegment StartX=-12.5599 StartY=30.1711 StartZ=0 EndX=12.5599 EndY=30.1711 EndZ=0
    g1: LineSegment StartX=12.5599 StartY=30.1711 StartZ=0 EndX=11.0709 EndY=23.1711 EndZ=0
    g2: LineSegment StartX=11.0709 StartY=23.1711 StartZ=0 EndX=-11.0709 EndY=23.1711 EndZ=0
    g3: LineSegment StartX=-11.0709 StartY=23.1711 StartZ=0 EndX=-12.5599 EndY=30.1711 EndZ=0
  constraints (9):
    c: Horizontal(g0)
    c: Coincident(g0,g1)
    c: Coincident(g1,g2)
    c: Horizontal(g2)
    c: Coincident(g2,g3)
    c: Coincident(g3,g0)
    c: Symmetric(g0,g0,g-2)
    c: Symmetric(g1,g2,g-2)
    c: DistanceY(g1,g0) = 7
FEATURE [PartDesign::Pad] Pad006
  Length = 21
  Length2 = 100
  Placement = pos=(0,0,-1.6) rot=(0,0,1;0rad)
  Profile = -> Sketch011
  Type = 0
FEATURE [Part::Cylinder] Cylinder028  label="Taladro1"
  Angle = 360
  AttacherType = Attacher::AttachEngine3D
  Height = 10
  Placement = pos=(-10.5,-5,2.3) rot=(0,0,1;0rad)
  Radius = 1.5
FEATURE [Part::Cylinder] Cylinder029  label="Taladro002"
  Angle = 360
  AttacherType = Attacher::AttachEngine3D
  Height = 10
  Placement = pos=(-10.5,-14,2.3) rot=(0,0,1;0rad)
  Radius = 1.5
FEATURE [Part::Cylinder] Cylinder030  label="Taladro003"
  Angle = 360
  AttacherType = Attacher::AttachEngine3D
  Height = 10
  Placement = pos=(10.5,-5,2.3) rot=(0,0,1;0rad)
  Radius = 1.5
FEATURE [Part::Cylinder] Cylinder031  label="Taladro004"
  Angle = 360
  AttacherType = Attacher::AttachEngine3D
  Height = 10
  Placement = pos=(10.5,-14,2.3) rot=(0,0,1;0rad)
  Radius = 1.5
FEATURE [Part::Cylinder] Cylinder032  label="Taladro005"
  Angle = 360
  AttacherType = Attacher::AttachEngine3D
  Height = 11
  Placement = pos=(-8.5,26.5,-1.7) rot=(0,0,1;0rad)
  Radius = 1.5
FEATURE [Part::Cylinder] Cylinder033  label="Taladro006"
  Angle = 360
  AttacherType = Attacher::AttachEngine3D
  Height = 11
  Placement = pos=(8.5,26.5,-1.7) rot=(0,0,1;0rad)
  Radius = 1.5
FEATURE [Part::MultiFuse] Fusion014  label="Taladros A"
  Placement = pos=(0,0,1) rot=(0,0,1;0rad)
  Shapes = -> [Cylinder028,Cylinder029,Cylinder030,Cylinder031,Cylinder032,Cylinder033]
FEATURE [Part::Cylinder] Cylinder034  label="Taladro007"
  Angle = 360
  AttacherType = Attacher::AttachEngine3D
  Height = 10
  Placement = pos=(-10.5,-5,-1) rot=(0,0,1;0rad)
  Radius = 1.5
FEATURE [Part::Cylinder] Cylinder035  label="Taladro008"
  Angle = 360
  AttacherType = Attacher::AttachEngine3D
  Height = 10
  Placement = pos=(-10.5,-14,-1) rot=(0,0,1;0rad)
  Radius = 1.5
FEATURE [Part::Cylinder] Cylinder036  label="Taladro009"
  Angle = 360
  AttacherType = Attacher::AttachEngine3D
  Height = 10
  Placement = pos=(10.5,-5,-1) rot=(0,0,1;0rad)
  Radius = 1.5
FEATURE [Part::Cylinder] Cylinder037  label="Taladro010"
  Angle = 360
  AttacherType = Attacher::AttachEngine3D
  Height = 10
  Placement = pos=(10.5,-14,-1) rot=(0,0,1;0rad)
  Radius = 1.5
FEATURE [Part::Cylinder] Cylinder038  label="Taladro011"
  Angle = 360
  AttacherType = Attacher::AttachEngine3D
  Height = 10
  Placement = pos=(-8.5,26.5,-1) rot=(0,0,1;0rad)
  Radius = 1
FEATURE [Part::Cylinder] Cylinder039  label="Taladro012"
  Angle = 360
  AttacherType = Attacher::AttachEngine3D
  Height = 10
  Placement = pos=(8.5,26.5,-1) rot=(0,0,1;0rad)
  Radius = 1
FEATURE [Part::MultiFuse] Fusion015  label="Taladros B"
  Shapes = -> [Cylinder034,Cylinder035,Cylinder036,Cylinder037,Cylinder038,Cylinder039]
FEATURE [Part::MultiFuse] Fusion016  label="Verticales Inferior"
  Shapes = -> [Box006,Box007,Pad006]
FEATURE [Part::Cut] Cut007  label="Verticales taladradas 1"
  Base = -> Fusion016
  Tool = -> Fusion014
FEATURE [Part::Cylinder] Cylinder040  label="Taladro013"
  Angle = 360
  AttacherType = Attacher::AttachEngine3D
  Height = 10
  Placement = pos=(0,-19,14) rot=(0,0,1;0rad)
  Radius = 0.7
FEATURE [Part::Cylinder] Cylinder041  label="Taladro014"
  Angle = 360
  AttacherType = Attacher::AttachEngine3D
  Height = 10
  Placement = pos=(0,8.2,14) rot=(0,0,1;0rad)
  Radius = 0.7
FEATURE [Sketcher::SketchObject] Sketch012
  MapMode = 5
  Placement = pos=(0,38,3) rot=(1,0,0;1.5708rad)
  sketch-geometry (1):
    g0: Circle CenterX=0 CenterY=10.1022 CenterZ=0 NormalX=0 NormalY=0 NormalZ=1 AngleXU=0 Radius=5
  constraints (2):
    c: PointOnObject(g0,g-2)
    c: Radius(g0) = 5
FEATURE [PartDesign::Pad] Pad007  label="Taladro 8mm"
  Length = 30
  Length2 = 100
  Placement = pos=(0,38,3) rot=(1,0,0;1.5708rad)
  Profile = -> Sketch012
  Type = 0
FEATURE [Mesh::Feature] servo_arm
  Placement = pos=(0,0,0) rot=(1,0,0;3.14159rad)
FEATURE [Part::Feature] servo_arm001
  shape: bbox 35.52 x 12.04 x 4.7 mm, 716 faces, 0 solids (baked)
FEATURE [Part::Feature] servo_arm001_solid  label="servo_arm001 (Solid)"
  shape: bbox 35.52 x 12.04 x 4.7 mm, 716 faces (baked)
FEATURE [Part::Feature] servo_arm001_solid001  label="brazo 1"
  Placement = pos=(0,11.8,0) rot=(-0.707107,0.707107,0;3.14159rad)
  shape: bbox 12.04 x 35.52 x 4.7 mm, 180 faces (baked)
FEATURE [Sketcher::SketchObject] Sketch014
  MapMode = 5
  sketch-geometry (13):
    g0: LineSegment StartX=-6.25 StartY=21.2197 StartZ=0 EndX=-3.1 EndY=21.2197 EndZ=0
    g1: LineSegment StartX=6.25 StartY=21.2197 StartZ=0 EndX=6.25 EndY=7.21967 EndZ=0
    g2: LineSegment StartX=-6.25 StartY=7.21963 StartZ=0 EndX=-6.25 EndY=21.2197 EndZ=0
    g3: LineSegment StartX=-3.1 StartY=21.2197 StartZ=0 EndX=-3.1 EndY=11.0427 EndZ=0
    g4: LineSegment StartX=3.1 StartY=21.2197 StartZ=0 EndX=3.1 EndY=11.0427 EndZ=0
    g5: LineSegment StartX=-1.1 StartY=9.04275 StartZ=0 EndX=1.1 EndY=9.04275 EndZ=0
    g6: ArcOfCircle CenterX=-1.1 CenterY=11.0427 CenterZ=0 NormalX=0 NormalY=0 NormalZ=1 AngleXU=0 Radius=2 StartAngle=3.14159 EndAngle=4.71239
    g7: ArcOfCircle CenterX=1.1 CenterY=11.0427 CenterZ=0 NormalX=0 NormalY=0 NormalZ=1 AngleXU=0 Radius=2 StartAngle=4.71239 EndAngle=6.28319
    g8: LineSegment StartX=3.1 StartY=21.2197 StartZ=0 EndX=6.25 EndY=21.2197 EndZ=0
    g9: Circle CenterX=0 CenterY=0 CenterZ=0 NormalX=0 NormalY=0 NormalZ=1 AngleXU=0 Radius=3.55
    g10: LineSegment StartX=-6.25 StartY=7.21963 StartZ=0 EndX=-6 EndY=1.25123e-07 EndZ=0
    g11: LineSegment StartX=6.25 StartY=7.21967 StartZ=0 EndX=5.99651 EndY=-0.204713 EndZ=0
    g12: ArcOfCircle CenterX=0 CenterY=0 CenterZ=0 NormalX=0 NormalY=0 NormalZ=1 AngleXU=0 Radius=6 StartAngle=3.14159 EndAngle=6.24906
  constraints (31):
    c: Coincident(g8,g1)
    c: Coincident(g2,g0)
    c: Vertical(g1)
    c: Vertical(g2)
    c: Symmetric(g0,g8,g-2)
    c: DistanceX(g0,g8) = 12.5
    c: DistanceY(g1,g8) = 14
    c: Vertical(g3)
    c: Vertical(g4)
    c: Horizontal(g5)
    c: Tangent(g3,g6) = -1.5708
    c: Tangent(g5,g6) = -1.5708
    c: Tangent(g4,g7) = 1.5708
    c: Tangent(g5,g7) = -1.5708
    c: Radius(g7) = 2
    c: Equal(g6,g7)
    c: Coincident(g0,g3)
    c: Coincident(g8,g4)
    c: Tangent(g0,g8)
    c: Coincident(g9,g-1)
    c: Coincident(g10,g2)
    c: Coincident(g11,g1)
    c: Coincident(g12,g-1)
    c: Coincident(g12,g11)
    c: Coincident(g12,g10)
    c: Tangent(g11,g12)
    c: Radius(g9) = 3.55
    c: Radius(g12) = 6
    c: DistanceY(g11,g1) = 7.42438
    c: DistanceX(g0,g0) = 3.15
    c: Symmetric(g0,g4,g-2)
FEATURE [Part::Extrusion] Extrude004  label="Horquilla base"
  Base = -> Sketch014
  Dir = (0,0,4.7)
  DirMode = 0
  FaceMakerClass = Part::FaceMakerExtrusion
  LengthFwd = 0
  LengthRev = 0
  Solid = true
  Symmetric = false
FEATURE [Sketcher::SketchObject] Sketch015
  MapMode = 5
  Placement = pos=(0,0,4.7) rot=(0,0,1;0rad)
  Support = -> [Extrude004]
  sketch-geometry (4):
    g0: ArcOfCircle CenterX=0 CenterY=0 CenterZ=0 NormalX=0 NormalY=0 NormalZ=1 AngleXU=0 Radius=3.55 StartAngle=2.49108 EndAngle=6.9337
    g1: LineSegment StartX=-2.825 StartY=2.14985 StartZ=0 EndX=-2.4 EndY=9.91968 EndZ=0
    g2: LineSegment StartX=2.825 StartY=2.14985 StartZ=0 EndX=2.4 EndY=9.91968 EndZ=0
    g3: LineSegment StartX=-2.4 StartY=9.91968 StartZ=0 EndX=2.4 EndY=9.91968 EndZ=0
  constraints (11):
    c: Coincident(g0,g-1)
    c: Coincident(g1,g0)
    c: Coincident(g2,g0)
    c: Coincident(g3,g1)
    c: Coincident(g3,g2)
    c: Horizontal(g3)
    c: Radius(g0) = 3.55
    c: Symmetric(g0,g0,g-2)
    c: DistanceX(g0,g0) = 5.65
    c: DistanceX(g1,g2) = 4.8
    c: Symmetric(g2,g1,g-2)
FEATURE [PartDesign::Pocket] Pocket  label="Horquilla 1"
  Length = 2
  Length2 = 100
  Profile = -> Sketch015
  Type = 0
FEATURE [PartDesign::Fillet] Fillet006  label="Horquilla"
  Base = -> Pocket [Edge44,Edge2]
  Radius = 2
FEATURE [Part::MultiFuse] Fusion019  label="Taladros C"
  Shapes = -> [Cylinder040,Cylinder041]
FEATURE [App::DocumentObjectGroup] Grupo004  label="Antiguos"
  Group = -> [Cut002,Grupo002,Pad005,Grupo005,servo_arm,servo_arm001,servo_arm001_solid,Extrude004,Pocket,servo_arm001_solid001,Fusion019,Fusion015]
FEATURE [Sketcher::SketchObject] Sketch016  label="Plano tapa inferior"
  MapMode = 5
  Placement = pos=(0,0,19) rot=(0,0,1;0rad)
  sketch-geometry (38):
    g0: LineSegment StartX=-29.5729 StartY=5.20224 StartZ=0 EndX=-9 EndY=13.3996 EndZ=0
    g1: LineSegment StartX=29.5878 StartY=-5.19626 StartZ=0 EndX=15.9802 EndY=-10.6636 EndZ=0
    g2: LineSegment StartX=-15.9802 StartY=-10.6636 StartZ=0 EndX=-29.5878 EndY=-5.19626 EndZ=0
    g3: Circle CenterX=27.5 CenterY=0 CenterZ=0 NormalX=0 NormalY=0 NormalZ=1 AngleXU=0 Radius=2.7
    g4: Circle CenterX=-27.5 CenterY=0 CenterZ=0 NormalX=0 NormalY=0 NormalZ=1 AngleXU=0 Radius=2.7
    g5: ArcOfCircle CenterX=27.5 CenterY=0 CenterZ=0 NormalX=0 NormalY=0 NormalZ=1 AngleXU=0 Radius=5.6 StartAngle=5.09444 EndAngle=7.47523
    g6: ArcOfCircle CenterX=-27.5 CenterY=0 CenterZ=0 NormalX=0 NormalY=0 NormalZ=1 AngleXU=0 Radius=5.6 StartAngle=1.94997 EndAngle=4.33034
    g7: GeomPoint [constr] X=-16.9626 Y=-10.4932 Z=0
    g8: LineSegment StartX=14.0987 StartY=-13.4473 StartZ=0 EndX=14.0987 EndY=-18.9006 EndZ=0
    g9: LineSegment StartX=9.09871 StartY=-23.9006 StartZ=0 EndX=-9.09871 EndY=-23.9006 EndZ=0
    g10: LineSegment StartX=-14.0987 StartY=-18.9006 StartZ=0 EndX=-14.0987 EndY=-13.4473 EndZ=0
    g11: LineSegment StartX=-6.325 StartY=7.26165 StartZ=0 EndX=6.325 EndY=7.26165 EndZ=0
    g12: LineSegment StartX=6.325 StartY=7.26165 StartZ=0 EndX=6.325 EndY=-17.7383 EndZ=0
    g13: LineSegment StartX=6.325 StartY=-17.7383 StartZ=0 EndX=-6.325 EndY=-17.7383 EndZ=0
    g14: LineSegment StartX=-6.325 StartY=-17.7383 StartZ=0 EndX=-6.325 EndY=7.26165 EndZ=0
    g15: ArcOfCircle CenterX=-9.09871 CenterY=-18.9006 CenterZ=0 NormalX=0 NormalY=0 NormalZ=1 AngleXU=0 Radius=5 StartAngle=3.14159 EndAngle=4.71239
    g16: ArcOfCircle CenterX=9.09871 CenterY=-18.9006 CenterZ=0 NormalX=0 NormalY=0 NormalZ=1 AngleXU=0 Radius=5 StartAngle=4.71239 EndAngle=6.28319
    g17: ArcOfCircle CenterX=-17.0987 CenterY=-13.4473 CenterZ=0 NormalX=0 NormalY=0 NormalZ=1 AngleXU=0 Radius=3 StartAngle=0 EndAngle=1.18875
    g18: ArcOfCircle CenterX=17.0987 CenterY=-13.4473 CenterZ=0 NormalX=0 NormalY=0 NormalZ=1 AngleXU=0 Radius=3 StartAngle=1.95284 EndAngle=3.14159
    g19: LineSegment StartX=-12.5409 StartY=30.1544 StartZ=0 EndX=12.5409 EndY=30.1544 EndZ=0
    g20: LineSegment StartX=-9 StartY=13.3996 StartZ=0 EndX=-12.5409 EndY=30.1544 EndZ=0
    g21: LineSegment StartX=9 StartY=13.3996 StartZ=0 EndX=12.5409 EndY=30.1544 EndZ=0
    g22: LineSegment StartX=9 StartY=13.3996 StartZ=0 EndX=29.5707 EndY=5.20311 EndZ=0
    g23: LineSegment [constr] StartX=-7.75 StartY=-18.3962 StartZ=0 EndX=-7.75 EndY=-1.18757 EndZ=0
    g24: LineSegment [constr] StartX=7.75 StartY=-1.18757 StartZ=0 EndX=7.75 EndY=-18.3962 EndZ=0
    g25: Circle CenterX=10.65 CenterY=-20.3343 CenterZ=0 NormalX=0 NormalY=0 NormalZ=1 AngleXU=0 Radius=1.5
    g26: Circle CenterX=-10.65 CenterY=-20.3343 CenterZ=0 NormalX=0 NormalY=0 NormalZ=1 AngleXU=0 Radius=1.5
    g27: Circle CenterX=13 CenterY=8.88628 CenterZ=0 NormalX=0 NormalY=0 NormalZ=1 AngleXU=0 Radius=1.5
    g28: Circle CenterX=-13 CenterY=8.88628 CenterZ=0 NormalX=0 NormalY=0 NormalZ=1 AngleXU=0 Radius=1.5
    g29: Circle CenterX=7.5 CenterY=20.1544 CenterZ=0 NormalX=0 NormalY=0 NormalZ=1 AngleXU=0 Radius=1.5
    g30: Circle CenterX=-7.5 CenterY=20.1544 CenterZ=0 NormalX=0 NormalY=0 NormalZ=1 AngleXU=0 Radius=1.5
    g31: Circle CenterX=0 CenterY=17.3339 CenterZ=0 NormalX=0 NormalY=0 NormalZ=1 AngleXU=0 Radius=5
    g32: Circle CenterX=0 CenterY=8.31883 CenterZ=0 NormalX=0 NormalY=0 NormalZ=1 AngleXU=0 Radius=0.7
    g33: Circle CenterX=0 CenterY=-18.8042 CenterZ=0 NormalX=0 NormalY=0 NormalZ=1 AngleXU=0 Radius=0.7
    g34: GeomPoint [constr] X=-12.5409 Y=30.1544 Z=0
    g35: GeomPoint [constr] X=-12.558 Y=30.1706 Z=0
    g36: LineSegment [constr] StartX=-9.50321 StartY=13.3971 StartZ=0 EndX=-8.71303 EndY=13.3971 EndZ=0
    g37: LineSegment [constr] StartX=-9.00746 StartY=13.8073 StartZ=0 EndX=-9.00746 EndY=13.1253 EndZ=0
  constraints (76):
    c: DistanceX(g4,g3) = 55
    c: Symmetric(g3,g4,g-2)
    c: PointOnObject(g3,g-1)
    c: Radius(g3) = 2.7
    c: Equal(g4,g3)
    c: Coincident(g5,g3)
    c: Coincident(g6,g4)
    c: Radius(g6) = 5.6
    c: Equal(g6,g5)
    c: Tangent(g1,g5) = 1.5708
    c: Tangent(g0,g6) = 1.5708
    c: Tangent(g2,g6) = 1.5708
    c: Horizontal(g9)
    c: Vertical(g8)
    c: Vertical(g10)
    c: Coincident(g11,g12)
    c: Coincident(g13,g14)
    c: Coincident(g14,g11)
    c: Horizontal(g11)
    c: Horizontal(g13)
    c: Vertical(g12)
    c: Vertical(g14)
    c: Symmetric(g12,g13,g-2)
    c: Tangent(g10,g15) = 1.5708
    c: Tangent(g9,g15) = 1.5708
    c: Tangent(g8,g16) = 1.5708
    c: Tangent(g9,g16) = 1.5708
    c: Radius(g15) = 5
    c: Equal(g16,g15)
    c: Tangent(g2,g17) = -1.5708
    c: Tangent(g10,g17) = -1.5708
    c: Tangent(g1,g18) = -1.5708
    c: Tangent(g8,g18) = -1.5708
    c: Radius(g18) = 3
    c: Equal(g18,g17)
    c: Symmetric(g10,g8,g-2)
    c: Horizontal(g19)
    c: Coincident(g20,g0)
    c: Coincident(g20,g19)
    c: Coincident(g21,g19)
    c: Symmetric(g19,g19,g-2)
    c: Coincident(g22,g21)
    c: Coincident(g22,g5)
    c: Symmetric(g21,g0,g-2)
    c: DistanceX(g0,g21) = 18
    c: Vertical(g23)
    c: Vertical(g24)
    c: Equal(g23,g24)
    c: Symmetric(g23,g24,g-2)
    c: DistanceX(g23,g24) = 15.5
    c: Radius(g25) = 1.5
    c: Equal(g26,g25)
    c: Symmetric(g26,g25,g-2)
    c: DistanceX(g26,g25) = 21.3
    c: Radius(g27) = 1.5
    c: Equal(g30,g29)
    c: Equal(g29,g28)
    c: Equal(g28,g27)
    c: Symmetric(g30,g29,g-2)
    c: Symmetric(g27,g28,g-2)
    c: DistanceX(g28,g27) = 26
    c: DistanceX(g30,g29) = 15
    c: PointOnObject(g31,g-2)
    c: Radius(g31) = 5
    c: DistanceY(g30,g19) = 10
    c: DistanceY(g12,g11) = 25
    c: DistanceX(g11,g11) = 12.65
    c: Radius(g33) = 0.7
    c: PointOnObject(g33,g-2)
    c: Equal(g33,g32)
    c: PointOnObject(g32,g-2)
    c: DistanceY(g33,g32) = 27.123
    c: Coincident(g34,g19)
    c: Horizontal(g36)
    c: Vertical(g37)
    c: Coincident(g13,g12)
FEATURE [PartDesign::Pad] Pad009  label="Base tapa inferior"
  Length = 4.8
  Length2 = 100
  Placement = pos=(0,0,19) rot=(0,0,1;0rad)
  Profile = -> Sketch016
  Type = 0
FEATURE [Part::Cut] Cut009  label="Verticales taladradas 2"
  Base = -> Cut007
  Tool = -> Pad007
FEATURE [Part::MultiFuse] Fusion020  label="Carter inferior"
  Shapes = -> [Pad009,Cut009]
FEATURE [Part::Cylinder] Cylinder042  label="Taladro015"
  Angle = 360
  AttacherType = Attacher::AttachEngine3D
  Height = 27
  Placement = pos=(-8.5,26.5,-1.7) rot=(0,0,1;0rad)
  Radius = 1.5
FEATURE [Part::Cylinder] Cylinder043  label="Taladro016"
  Angle = 360
  AttacherType = Attacher::AttachEngine3D
  Height = 27
  Placement = pos=(8.5,26.5,-1.7) rot=(0,0,1;0rad)
  Radius = 1.5
FEATURE [Part::MultiFuse] Fusion021  label="Seg taladros A"
  Shapes = -> [Cylinder042,Cylinder043]
FEATURE [Part::Cut] Cut010  label="Carter inf 2"
  Base = -> Fusion020
  Tool = -> Fusion021
FEATURE [App::DocumentObjectGroup] Grupo006  label="Carter"
  Group = -> [Pad,Cut010]
